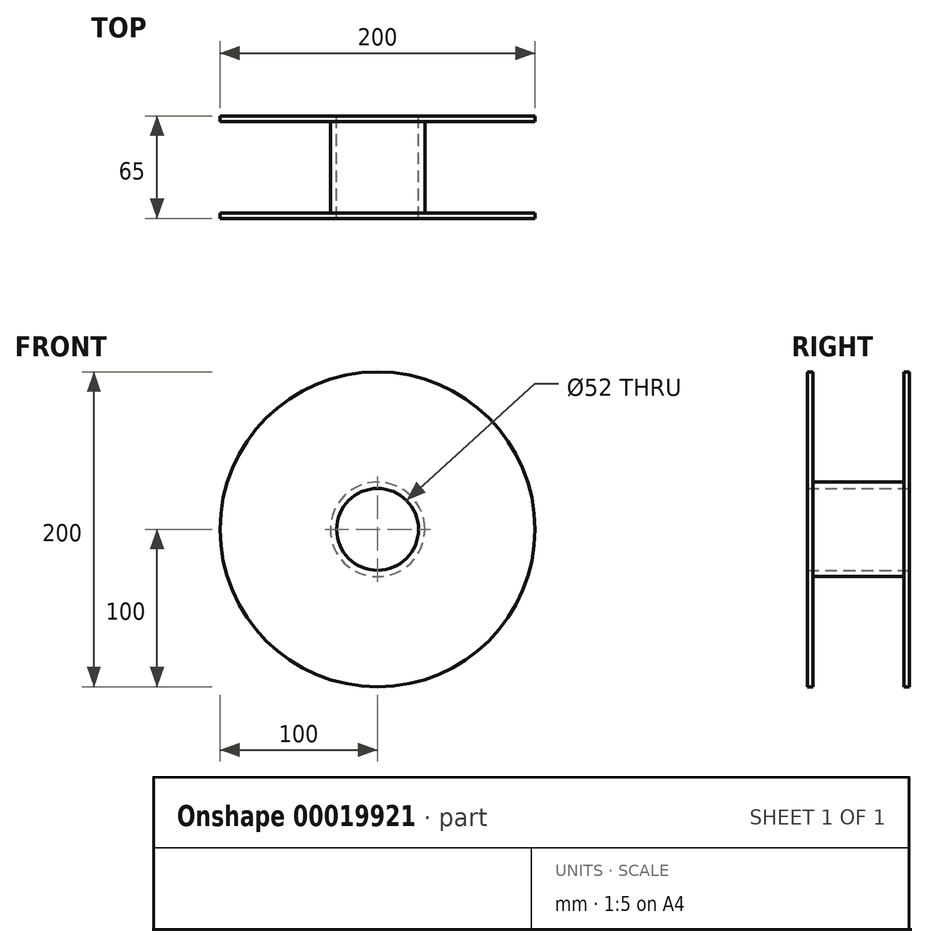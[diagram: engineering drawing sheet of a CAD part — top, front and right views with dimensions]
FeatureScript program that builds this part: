
annotation { "Feature Type Name" : "Feature", "Feature Type Description" : "" }
export const myFeature = defineFeature(function(context is Context, id is Id, definition is map)
    precondition{}
    {
        {
            var Q0;
            Q0=qCreatedBy(makeId("Front.planeOp"),FACE);
            var sketch = newSketch(context, id + "F0", { "sketchPlane" : qUnion([Q0])});
            skCircle(sketch, "E0", {"center": v(0, 0) * mm, "radius": 100 * mm});
            skCircle(sketch, "E1", {"center": v(0, 0) * mm, "radius": 26 * mm});
            skSolve(sketch);
        }
        {
            var Q0;
            Q0=qSketchRegion(id+"F0",true);
            extrude(context, id + "F1", {"entities" : qUnion([Q0]), "endBound" : BoundingType.SYMMETRIC, "depth" : 65 * mm});
        }
        {
            var Q0;
            Q0=qCreatedBy(makeId("Top.planeOp"),FACE);
            var sketch = newSketch(context, id + "F2", { "sketchPlane" : qUnion([Q0])});
            skLineSegment(sketch, "E2", {"start": v(0, 0) * mm, "end": v(0, 21.03) * mm, "construction": true});
            skLineSegment(sketch, "E3.bottom", {"start": v(30, 29) * mm, "end": v(130, 29) * mm});
            skLineSegment(sketch, "E3.top", {"start": v(30, -29) * mm, "end": v(130, -29) * mm});
            skLineSegment(sketch, "E3.left", {"start": v(30, 29) * mm, "end": v(30, -29) * mm});
            skLineSegment(sketch, "E3.right", {"start": v(130, 29) * mm, "end": v(130, -29) * mm});
            skLineSegment(sketch, "E4", {"start": v(0, 0) * mm, "end": v(41.92, 0) * mm, "construction": true});
            skSolve(sketch);
        }
        {
            var Q0;
            Q0=qSketchRegion(id+"F2",true);
            var Q1;
            Q1=sQuery(id+"F2.wireOp",EDGE,"E2");
            revolve(context, id + "F3", {"operationType" : NewBodyOperationType.REMOVE, "entities" : qUnion([Q0]), "axis" : qUnion([Q1]), "revolveType" : RevolveType.FULL, "oppositeDirection" : true});
        }
    });
